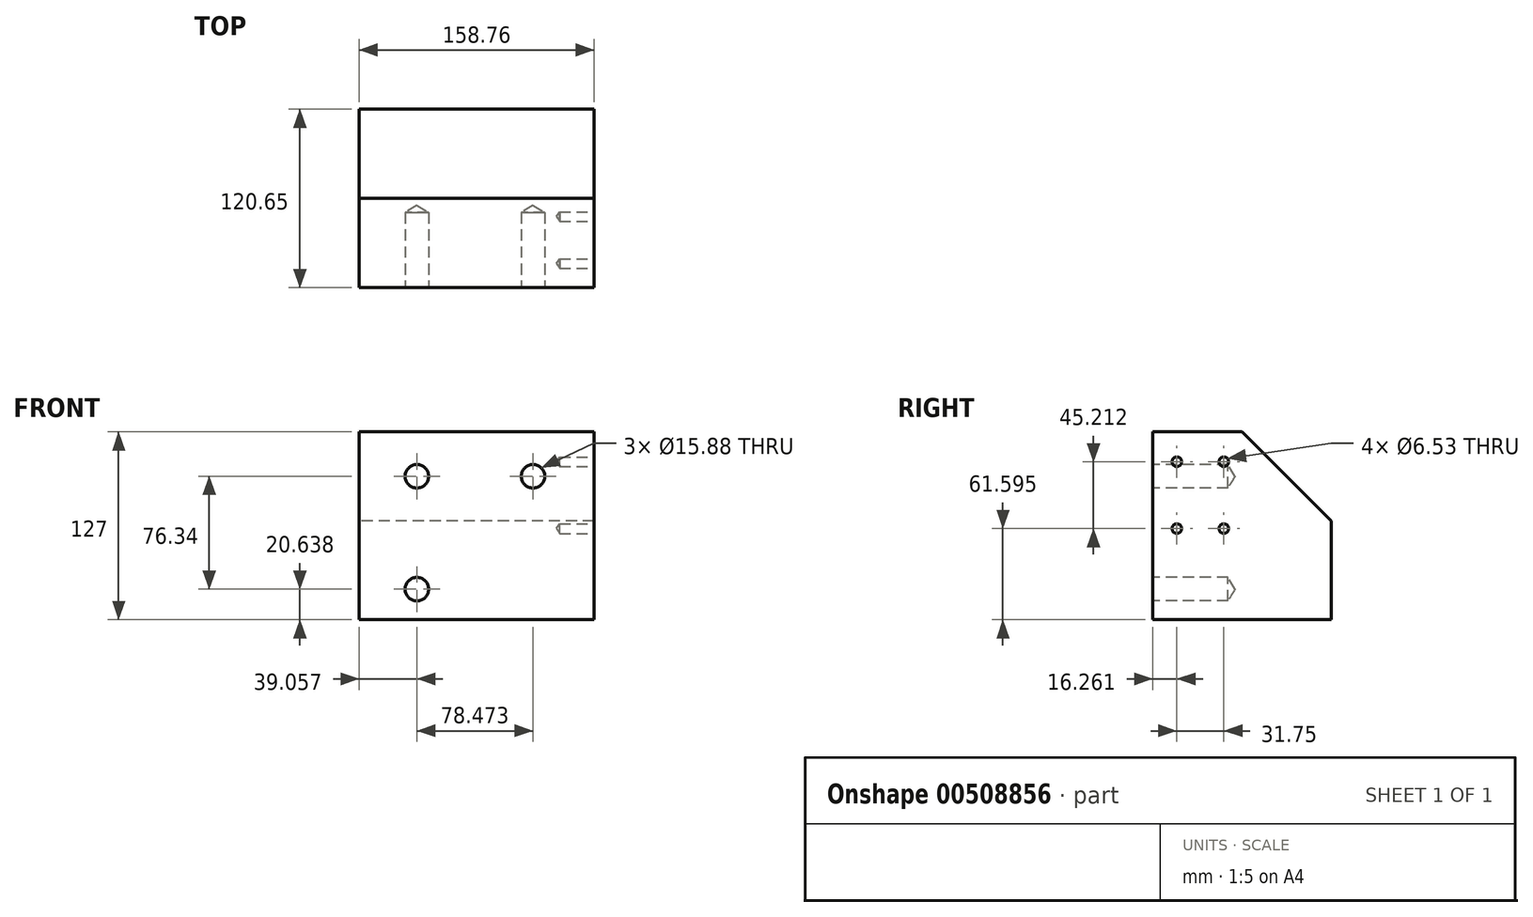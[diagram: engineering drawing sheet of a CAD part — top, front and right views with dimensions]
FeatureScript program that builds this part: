
annotation { "Feature Type Name" : "Feature", "Feature Type Description" : "" }
export const myFeature = defineFeature(function(context is Context, id is Id, definition is map)
    precondition{}
    {
        {
            var Q0;
            Q0=qCreatedBy(makeId("Right.planeOp"),FACE);
            var sketch = newSketch(context, id + "F0", { "sketchPlane" : qUnion([Q0])});
            skLineSegment(sketch, "E0", {"start": v(-60.33, -63.5) * mm, "end": v(-60.33, 63.5) * mm});
            skLineSegment(sketch, "E1", {"start": v(-60.33, 63.5) * mm, "end": v(0, 63.5) * mm});
            skLineSegment(sketch, "E2", {"start": v(0, 63.5) * mm, "end": v(60.32, 3.18) * mm});
            skLineSegment(sketch, "E3", {"start": v(60.32, 3.18) * mm, "end": v(60.33, -63.5) * mm});
            skLineSegment(sketch, "E4", {"start": v(60.32, -63.5) * mm, "end": v(-60.33, -63.5) * mm});
            skSolve(sketch);
        }
        {
            var Q0;
            Q0=makeQuery(id+"F0.imprint","IMPRINT",FACE,{"disambiguationData":[TD([[makeQuery(id+"F0.imprint","IMPRINT",EDGE,{"derivedFrom":sQuery(id+"F0.wireOp",EDGE,"E0")}),-1.0]])]});
            extrude(context, id + "F1", {"entities" : qUnion([Q0]), "endBound" : BoundingType.SYMMETRIC, "depth" : 158.75 * mm});
        }
        {
            var Q0;
            Q0=makeQuery(id+"F1.opExtrude","SWEPT_FACE",FACE,{"disambiguationData":[OSD([sQuery(id+"F0.wireOp",EDGE,"E0")])]});
            var sketch = newSketch(context, id + "F2", { "sketchPlane" : qUnion([Q0])});
            skPoint(sketch, "E5", {"position": v(-40.32, 33.48) * mm});
            skPoint(sketch, "E6", {"position": v(-40.32, -42.86) * mm});
            skPoint(sketch, "E7", {"position": v(38.15, 33.48) * mm});
            skSolve(sketch);
        }
        {
            var Q0;
            Q0=sQuery(id+"F2.wireOp",VERTEX,"E6");
            var Q1;
            Q1=sQuery(id+"F2.wireOp",VERTEX,"E5");
            var Q2;
            Q2=sQuery(id+"F2.wireOp",VERTEX,"E7");
            var Q3;
            Q3=makeQuery(id+"F1.opExtrude","SWEPT_BODY",BODY,{"disambiguationData":[OSD([sQuery(id+"F0.wireOp",EDGE,"E0"),sQuery(id+"F0.wireOp",EDGE,"E1"),sQuery(id+"F0.wireOp",EDGE,"E2"),sQuery(id+"F0.wireOp",EDGE,"E3"),sQuery(id+"F0.wireOp",EDGE,"E4")])]});
            hole(context, id + "F3", {"style" : HoleStyle.SIMPLE, "endStyle" : HoleEndStyle.BLIND, "holeDiameter" : 15.88 * mm, "holeDepth" : 50.8 * mm, "isTappedThrough" : true, "tappedDepth" : 31.75 * mm, "tapClearance" : 3, "locations" : qUnion([Q0, Q1, Q2]), "scope" : qUnion([Q3])});
        }
        {
            var Q0;
            Q0=makeQuery(id+"F1.opExtrude","CAP_FACE",FACE,{"disambiguationData":[OSD([sQuery(id+"F0.wireOp",EDGE,"E0"),sQuery(id+"F0.wireOp",EDGE,"E1"),sQuery(id+"F0.wireOp",EDGE,"E2"),sQuery(id+"F0.wireOp",EDGE,"E3"),sQuery(id+"F0.wireOp",EDGE,"E4")])],"isStart":false});
            var sketch = newSketch(context, id + "F4", { "sketchPlane" : qUnion([Q0])});
            skPoint(sketch, "E8", {"position": v(-44.07, 43.3) * mm});
            skPoint(sketch, "E9", {"position": v(-44.07, -1.9) * mm});
            skPoint(sketch, "E10", {"position": v(-12.32, -1.9) * mm});
            skPoint(sketch, "E11", {"position": v(-12.32, 43.3) * mm});
            skSolve(sketch);
        }
        {
            var Q0;
            Q0=sQuery(id+"F4.wireOp",VERTEX,"E8");
            var Q1;
            Q1=sQuery(id+"F4.wireOp",VERTEX,"E9");
            var Q2;
            Q2=sQuery(id+"F4.wireOp",VERTEX,"E10");
            var Q3;
            Q3=sQuery(id+"F4.wireOp",VERTEX,"E11");
            var Q4;
            Q4=makeQuery(id+"F1.opExtrude","SWEPT_BODY",BODY,{"disambiguationData":[OSD([sQuery(id+"F0.wireOp",EDGE,"E0"),sQuery(id+"F0.wireOp",EDGE,"E1"),sQuery(id+"F0.wireOp",EDGE,"E2"),sQuery(id+"F0.wireOp",EDGE,"E3"),sQuery(id+"F0.wireOp",EDGE,"E4")])]});
            hole(context, id + "F5", {"style" : HoleStyle.SIMPLE, "endStyle" : HoleEndStyle.BLIND, "standardTappedOrClearance" : lookupTablePath({ "standard" : "ANSI", "engagement" : "75%", "pitch" : "18 tpi", "size" : "5/16", "type" : "Tapped" }), "standardBlindInLast" : lookupTablePath({ "standard" : "ANSI", "engagement" : "75%", "pitch" : "18 tpi", "size" : "5/16", "type" : "Tapped" }), "holeDiameter" : 6.53 * mm, "showTappedDepth" : true, "holeDepth" : 23.28 * mm, "isTappedThrough" : true, "tappedDepth" : 19.05 * mm, "tapClearance" : 3, "locations" : qUnion([Q0, Q1, Q2, Q3]), "scope" : qUnion([Q4]), "majorDiameter" : 7.94 * mm});
        }
    });
